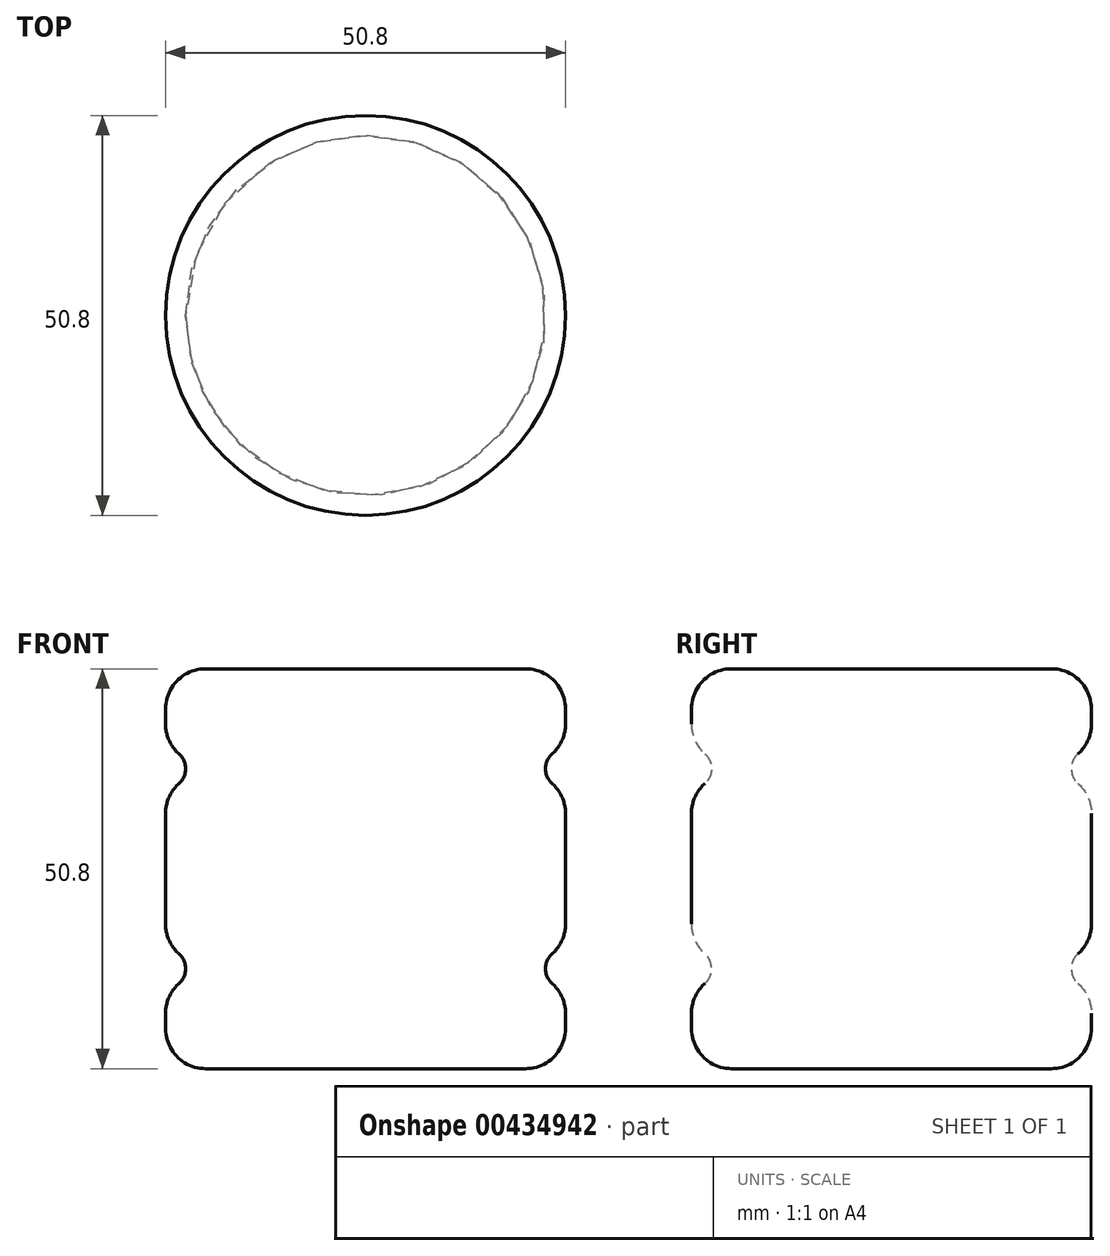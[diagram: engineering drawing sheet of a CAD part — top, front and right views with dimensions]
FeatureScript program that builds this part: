
annotation { "Feature Type Name" : "Feature", "Feature Type Description" : "" }
export const myFeature = defineFeature(function(context is Context, id is Id, definition is map)
    precondition{}
    {
        {
            var Q0;
            Q0=qCreatedBy(makeId("Front.planeOp"),FACE);
            var sketch = newSketch(context, id + "F0", { "sketchPlane" : qUnion([Q0])});
            skLineSegment(sketch, "E0", {"start": v(0, 0) * mm, "end": v(0, 50.8) * mm});
            skLineSegment(sketch, "E1", {"start": v(0, 50.8) * mm, "end": v(25.4, 50.8) * mm});
            skLineSegment(sketch, "E2", {"start": v(25.4, 50.8) * mm, "end": v(25.4, 15.24) * mm});
            skLineSegment(sketch, "E3", {"start": v(25.4, 0) * mm, "end": v(0, 0) * mm});
            skArc(sketch, "E4", {"start": v(25.4, 40.64) * mm, "mid": v(22.86, 38.1) * mm, "end": v(25.4, 35.56) * mm});
            skArc(sketch, "E5", {"start": v(25.4, 15.24) * mm, "mid": v(22.86, 12.7) * mm, "end": v(25.4, 10.16) * mm});
            skPoint(sketch, "E6.orphan", {"position": v(36.28, 38.1) * mm});
            skPoint(sketch, "E7.end.orphan", {"position": v(36.28, 0) * mm});
            skLineSegment(sketch, "E8.trimOffspring", {"start": v(25.4, 10.16) * mm, "end": v(25.4, 0) * mm});
            skSolve(sketch);
        }
        {
            var Q0;
            Q0=makeQuery(id+"F0.imprint","IMPRINT",FACE,{"disambiguationData":[TD([[makeQuery(id+"F0.imprint","IMPRINT",EDGE,{"derivedFrom":sQuery(id+"F0.wireOp",EDGE,"E0")}),-1.0]])]});
            var Q1;
            Q1=sQuery(id+"F0.wireOp",EDGE,"E0");
            revolve(context, id + "F1", {"entities" : qUnion([Q0]), "axis" : qUnion([Q1]), "revolveType" : RevolveType.FULL});
        }
        {
            var Q0;
            Q0=makeQuery(id+"F1.opRevolve","SWEPT_FACE",FACE,{"disambiguationData":[OSD([sQuery(id+"F0.wireOp",EDGE,"E1")])]});
            var Q1;
            Q1=makeQuery(id+"F1.opRevolve","SWEPT_FACE",FACE,{"disambiguationData":[OSD([sQuery(id+"F0.wireOp",EDGE,"E3")])]});
            var Q2;
            Q2=makeQuery(id+"F1.opRevolve","SWEPT_FACE",FACE,{"disambiguationData":[OSD([sQuery(id+"F0.wireOp",EDGE,"E5")])]});
            var Q3;
            Q3=makeQuery(id+"F1.opRevolve","SWEPT_FACE",FACE,{"disambiguationData":[OSD([sQuery(id+"F0.wireOp",EDGE,"E4")])]});
            fillet(context, id + "F2", {"entities" : qUnion([Q0, Q1, Q2, Q3]), "radius" : 5.08 * mm, "tangentPropagation" : true, "allowEdgeOverflow" : false});
        }
    });
